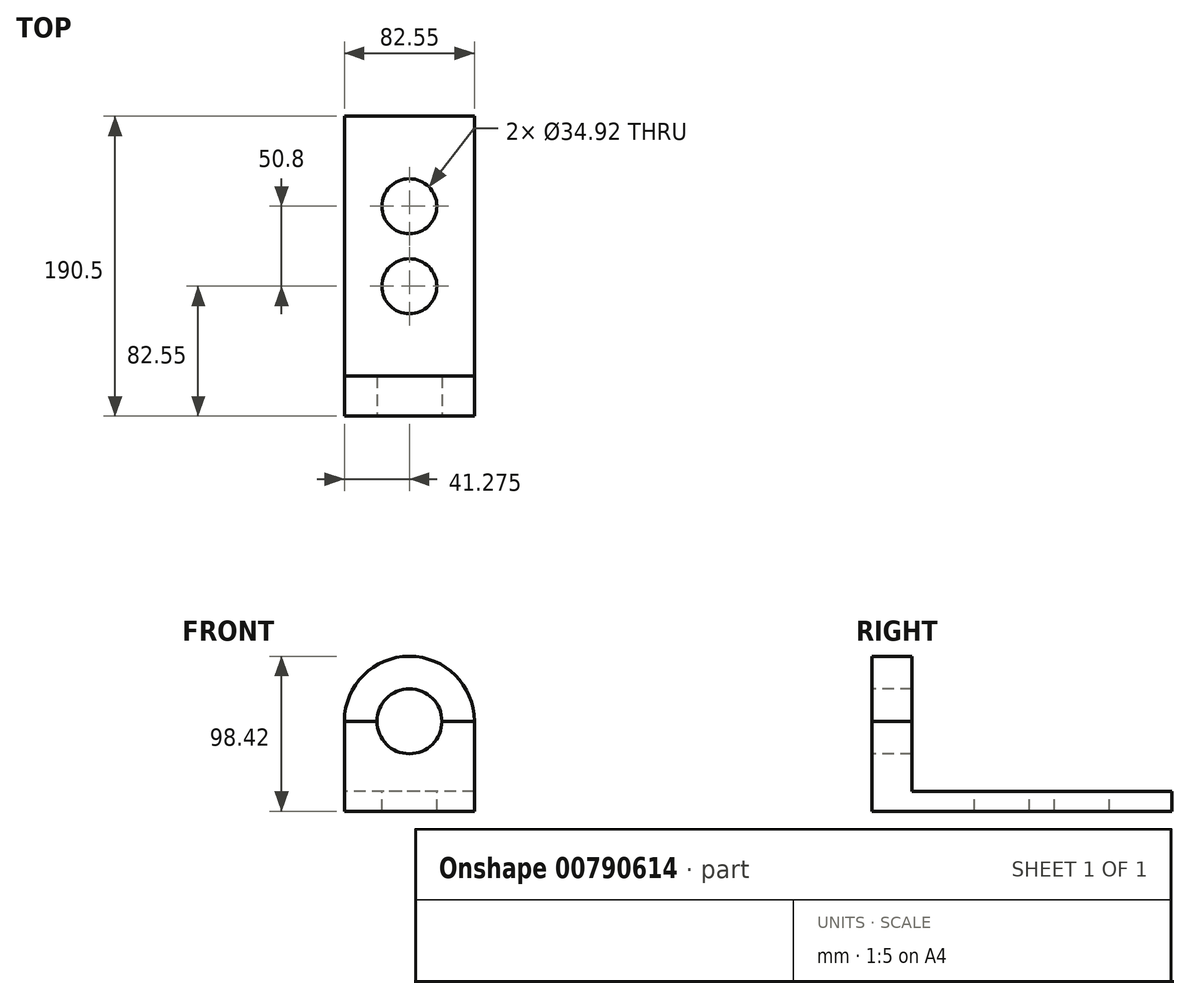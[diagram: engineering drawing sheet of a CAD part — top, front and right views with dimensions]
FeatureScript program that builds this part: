
annotation { "Feature Type Name" : "Feature", "Feature Type Description" : "" }
export const myFeature = defineFeature(function(context is Context, id is Id, definition is map)
    precondition{}
    {
        {
            var Q0;
            Q0=qCreatedBy(makeId("Right.planeOp"),FACE);
            var sketch = newSketch(context, id + "F0", { "sketchPlane" : qUnion([Q0])});
            skLineSegment(sketch, "E0", {"start": v(0, 0) * mm, "end": v(-190.5, 0) * mm});
            skLineSegment(sketch, "E1", {"start": v(-190.5, 0) * mm, "end": v(-190.5, 101.6) * mm});
            skLineSegment(sketch, "E2", {"start": v(-190.5, 101.6) * mm, "end": v(-165.1, 101.6) * mm});
            skLineSegment(sketch, "E3", {"start": v(-165.1, 101.6) * mm, "end": v(-165.1, 12.7) * mm});
            skLineSegment(sketch, "E4", {"start": v(-165.1, 12.7) * mm, "end": v(0, 12.7) * mm});
            skLineSegment(sketch, "E5", {"start": v(0, 12.7) * mm, "end": v(0, 0) * mm});
            skSolve(sketch);
        }
        {
            var Q0;
            Q0=makeQuery(id+"F0.imprint","IMPRINT",FACE,{"disambiguationData":[TD([[makeQuery(id+"F0.imprint","IMPRINT",EDGE,{"derivedFrom":sQuery(id+"F0.wireOp",EDGE,"E0")}),-1.0]])]});
            extrude(context, id + "F1", {"entities" : qUnion([Q0]), "depth" : 82.55 * mm, "offsetDistance" : 25.4 * mm});
        }
        {
            var Q0;
            Q0=makeQuery(id+"F1.opExtrude","SWEPT_FACE",FACE,{"disambiguationData":[OSD([sQuery(id+"F0.wireOp",EDGE,"E4")])]});
            var sketch = newSketch(context, id + "F2", { "sketchPlane" : qUnion([Q0])});
            skLineSegment(sketch, "E6", {"start": v(41.28, 0) * mm, "end": v(41.28, -57.15) * mm, "construction": true});
            skLineSegment(sketch, "E7", {"start": v(41.28, -165.1) * mm, "end": v(41.28, -107.95) * mm, "construction": true});
            skCircle(sketch, "E8", {"center": v(41.28, -107.95) * mm, "radius": 17.46 * mm});
            skCircle(sketch, "E9", {"center": v(41.28, -57.15) * mm, "radius": 17.46 * mm});
            skSolve(sketch);
        }
        {
            var Q0;
            Q0=makeQuery(id+"F2.imprint","IMPRINT",FACE,{"disambiguationData":[TD([[makeQuery(id+"F2.imprint","IMPRINT",EDGE,{"derivedFrom":sQuery(id+"F2.wireOp",EDGE,"E9")}),1.0]])]});
            var Q1;
            Q1=makeQuery(id+"F2.imprint","IMPRINT",FACE,{"disambiguationData":[TD([[makeQuery(id+"F2.imprint","IMPRINT",EDGE,{"derivedFrom":sQuery(id+"F2.wireOp",EDGE,"E8")}),1.0]])]});
            extrude(context, id + "F3", {"entities" : qUnion([Q0, Q1]), "operationType" : NewBodyOperationType.REMOVE, "endBound" : BoundingType.THROUGH_ALL, "oppositeDirection" : true, "depth" : 25.4 * mm, "offsetDistance" : 25.4 * mm});
        }
        {
            var Q0;
            Q0=makeQuery(id+"F1.opExtrude","SWEPT_FACE",FACE,{"disambiguationData":[OSD([sQuery(id+"F0.wireOp",EDGE,"E3")])]});
            var sketch = newSketch(context, id + "F4", { "sketchPlane" : qUnion([Q0])});
            skLineSegment(sketch, "E10", {"start": v(-82.55, 57.15) * mm, "end": v(0, 57.15) * mm});
            skSolve(sketch);
        }
        {
            var Q0;
            {var subQ0=sQuery(id+"F4.wireOp",EDGE,"E10");Q0=makeQuery(id+"F4.imprint","IMPRINT",FACE,{"disambiguationData":[TD([[makeQuery(id+"F4.imprint","IMPRINT",EDGE,{"derivedFrom":subQ0}),1.0]])]});}
            extrude(context, id + "F5", {"entities" : qUnion([Q0]), "operationType" : NewBodyOperationType.REMOVE, "endBound" : BoundingType.THROUGH_ALL, "oppositeDirection" : true, "depth" : 25.4 * mm, "offsetDistance" : 25.4 * mm});
        }
        {
            var Q0;
            Q0=makeQuery(id+"F1.opExtrude","SWEPT_FACE",FACE,{"disambiguationData":[OSD([sQuery(id+"F0.wireOp",EDGE,"E3")])]});
            var sketch = newSketch(context, id + "F6", { "sketchPlane" : qUnion([Q0])});
            skArc(sketch, "E11", {"start": v(0, 57.15) * mm, "mid": v(-41.28, 98.42) * mm, "end": v(-82.55, 57.15) * mm});
            skSolve(sketch);
        }
        {
            var Q0;
            Q0=makeQuery(id+"F6.imprint","IMPRINT",FACE,{"disambiguationData":[TD([[makeQuery(id+"F6.imprint","IMPRINT",EDGE,{"derivedFrom":sQuery(id+"F6.wireOp",EDGE,"E11")}),1.0]])]});
            extrude(context, id + "F7", {"entities" : qUnion([Q0]), "oppositeDirection" : true, "depth" : 25.4 * mm, "offsetDistance" : 25.4 * mm});
        }
        {
            var Q0;
            Q0=makeQuery(id+"F7.opExtrude","CAP_FACE",FACE,{"disambiguationData":[OSD([sQuery(id+"F4.wireOp",EDGE,"E10"),sQuery(id+"F6.wireOp",EDGE,"E11")])],"isStart":false});
            var sketch = newSketch(context, id + "F8", { "sketchPlane" : qUnion([Q0])});
            skCircle(sketch, "E12", {"center": v(41.28, 57.15) * mm, "radius": 20.64 * mm});
            skSolve(sketch);
        }
        {
            var Q0;
            Q0 = qSketchRegion(id + "F8", true);
            extrude(context, id + "F9", {"entities" : qUnion([Q0]), "operationType" : NewBodyOperationType.REMOVE, "endBound" : BoundingType.THROUGH_ALL, "oppositeDirection" : true, "depth" : 25.4 * mm, "offsetDistance" : 25.4 * mm});
        }
        {
            var Q0;
            Q0=makeQuery(id+"F1.opExtrude","SWEPT_FACE",FACE,{"disambiguationData":[OSD([sQuery(id+"F0.wireOp",EDGE,"E1")])]});
            var sketch = newSketch(context, id + "F10", { "sketchPlane" : qUnion([Q0])});
            skCircle(sketch, "E13", {"center": v(41.28, 57.15) * mm, "radius": 20.43 * mm});
            skSolve(sketch);
        }
        {
            var Q0;
            Q0 = qSketchRegion(id + "F10", true);
            extrude(context, id + "F11", {"entities" : qUnion([Q0]), "operationType" : NewBodyOperationType.REMOVE, "oppositeDirection" : true, "depth" : 25.4 * mm, "offsetDistance" : 25.4 * mm});
        }
    });
